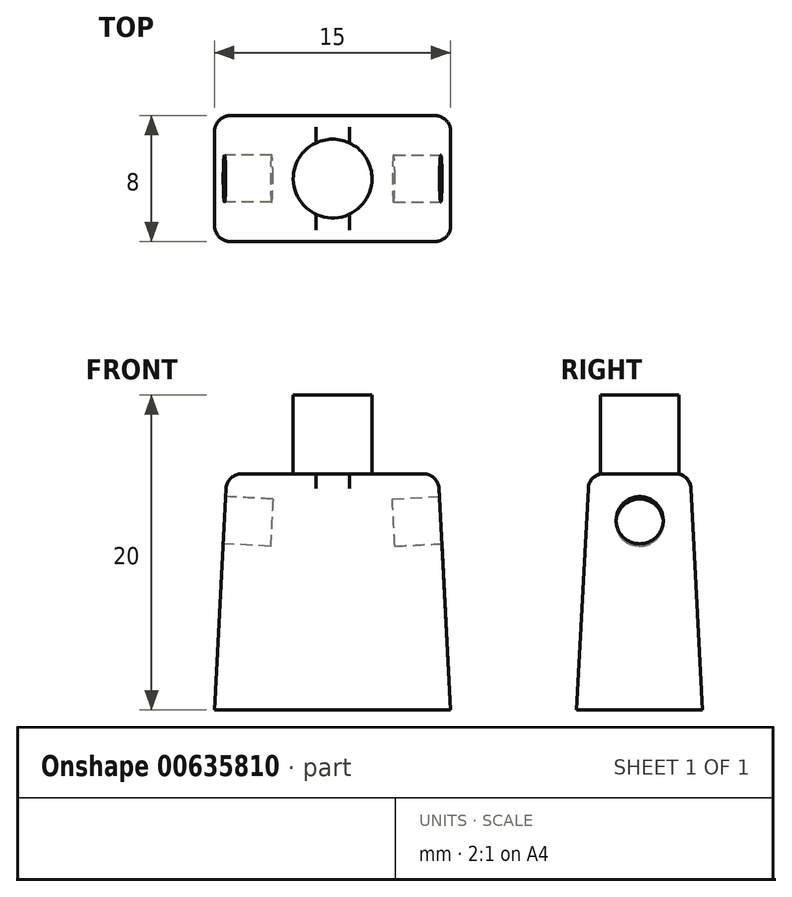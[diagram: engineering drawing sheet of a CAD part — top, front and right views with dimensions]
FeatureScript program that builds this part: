
annotation { "Feature Type Name" : "Feature", "Feature Type Description" : "" }
export const myFeature = defineFeature(function(context is Context, id is Id, definition is map)
    precondition{}
    {
        {
            var Q0;
            Q0=qCreatedBy(makeId("Top.planeOp"),FACE);
            var sketch = newSketch(context, id + "F0", { "sketchPlane" : qUnion([Q0])});
            skLineSegment(sketch, "E0.bottom", {"start": v(7.5, -4) * mm, "end": v(-7.5, -4) * mm});
            skLineSegment(sketch, "E0.top", {"start": v(7.5, 4) * mm, "end": v(-7.5, 4) * mm});
            skLineSegment(sketch, "E0.left", {"start": v(7.5, -4) * mm, "end": v(7.5, 4) * mm});
            skLineSegment(sketch, "E0.right", {"start": v(-7.5, -4) * mm, "end": v(-7.5, 4) * mm});
            skPoint(sketch, "E0.middle", {"position": v(0, 0) * mm});
            skSolve(sketch);
        }
        {
            var Q0;
            Q0 = qSketchRegion(id + "F0", true);
            extrude(context, id + "F1", {"entities" : qUnion([Q0]), "depth" : 15 * mm, "offsetDistance" : 25.4 * mm, "hasDraft" : true, "draftAngle" : 3 * degree, "draftPullDirection" : true});
        }
        {
            var Q0;
            Q0=makeQuery(id+"F1.opExtrude","CAP_FACE",FACE,{"disambiguationData":[OSD([sQuery(id+"F0.wireOp",EDGE,"E0.bottom"),sQuery(id+"F0.wireOp",EDGE,"E0.top"),sQuery(id+"F0.wireOp",EDGE,"E0.left"),sQuery(id+"F0.wireOp",EDGE,"E0.right")])],"isStart":false});
            var sketch = newSketch(context, id + "F2", { "sketchPlane" : qUnion([Q0])});
            skCircle(sketch, "E1", {"center": v(0, 0) * mm, "radius": 2.5 * mm});
            skSolve(sketch);
        }
        {
            var Q0;
            Q0 = qSketchRegion(id + "F2", true);
            extrude(context, id + "F3", {"entities" : qUnion([Q0]), "operationType" : NewBodyOperationType.ADD, "depth" : 5 * mm, "offsetDistance" : 25.4 * mm});
        }
        {
            var Q0;
            Q0=makeQuery(id+"F1.opExtrude","SWEPT_EDGE",EDGE,{"disambiguationData":[OSD([sQuery(id+"F0.wireOp",EDGE,"E0.bottom"),sQuery(id+"F0.wireOp",EDGE,"E0.right")])]});
            var Q1;
            Q1=makeQuery(id+"F1.opExtrude","CAP_EDGE",EDGE,{"disambiguationData":[OSD([sQuery(id+"F0.wireOp",EDGE,"E0.right")])],"isStart":false});
            var Q2;
            Q2=makeQuery(id+"F1.opExtrude","CAP_EDGE",EDGE,{"disambiguationData":[OSD([sQuery(id+"F0.wireOp",EDGE,"E0.bottom")])],"isStart":false});
            var Q3;
            Q3=makeQuery(id+"F1.opExtrude","SWEPT_EDGE",EDGE,{"disambiguationData":[OSD([sQuery(id+"F0.wireOp",EDGE,"E0.top"),sQuery(id+"F0.wireOp",EDGE,"E0.left")])]});
            var Q4;
            Q4=makeQuery(id+"F1.opExtrude","CAP_EDGE",EDGE,{"disambiguationData":[OSD([sQuery(id+"F0.wireOp",EDGE,"E0.top")])],"isStart":false});
            var Q5;
            Q5=makeQuery(id+"F1.opExtrude","SWEPT_EDGE",EDGE,{"disambiguationData":[OSD([sQuery(id+"F0.wireOp",EDGE,"E0.top"),sQuery(id+"F0.wireOp",EDGE,"E0.right")])]});
            var Q6;
            Q6=makeQuery(id+"F1.opExtrude","SWEPT_EDGE",EDGE,{"disambiguationData":[OSD([sQuery(id+"F0.wireOp",EDGE,"E0.bottom"),sQuery(id+"F0.wireOp",EDGE,"E0.left")])]});
            var Q7;
            Q7=makeQuery(id+"F1.opExtrude","CAP_EDGE",EDGE,{"disambiguationData":[OSD([sQuery(id+"F0.wireOp",EDGE,"E0.left")])],"isStart":false});
            fillet(context, id + "F4", {"entities" : qUnion([Q0, Q1, Q2, Q3, Q4, Q5, Q6, Q7]), "radius" : 1 * mm, "tangentPropagation" : true, "allowEdgeOverflow" : false});
        }
        {
            var Q0;
            Q0=makeQuery(id+"F1.opExtrude","SWEPT_FACE",FACE,{"disambiguationData":[OSD([sQuery(id+"F0.wireOp",EDGE,"E0.left")])]});
            var sketch = newSketch(context, id + "F5", { "sketchPlane" : qUnion([Q0])});
            skCircle(sketch, "E2", {"center": v(0, 11.68) * mm, "radius": 1.5 * mm});
            skSolve(sketch);
        }
        {
            var Q0;
            Q0 = qSketchRegion(id + "F5", true);
            extrude(context, id + "F6", {"entities" : qUnion([Q0]), "operationType" : NewBodyOperationType.REMOVE, "oppositeDirection" : true, "depth" : 3 * mm, "offsetDistance" : 25.4 * mm});
        }
        {
            var Q0;
            Q0=makeQuery(id+"F1.opExtrude","SWEPT_FACE",FACE,{"disambiguationData":[OSD([sQuery(id+"F0.wireOp",EDGE,"E0.right")])]});
            var sketch = newSketch(context, id + "F7", { "sketchPlane" : qUnion([Q0])});
            skCircle(sketch, "E3", {"center": v(0, 11.68) * mm, "radius": 1.5 * mm});
            skSolve(sketch);
        }
        {
            var Q0;
            Q0 = qSketchRegion(id + "F7", true);
            extrude(context, id + "F8", {"entities" : qUnion([Q0]), "operationType" : NewBodyOperationType.REMOVE, "oppositeDirection" : true, "depth" : 3 * mm, "offsetDistance" : 25.4 * mm});
        }
    });
